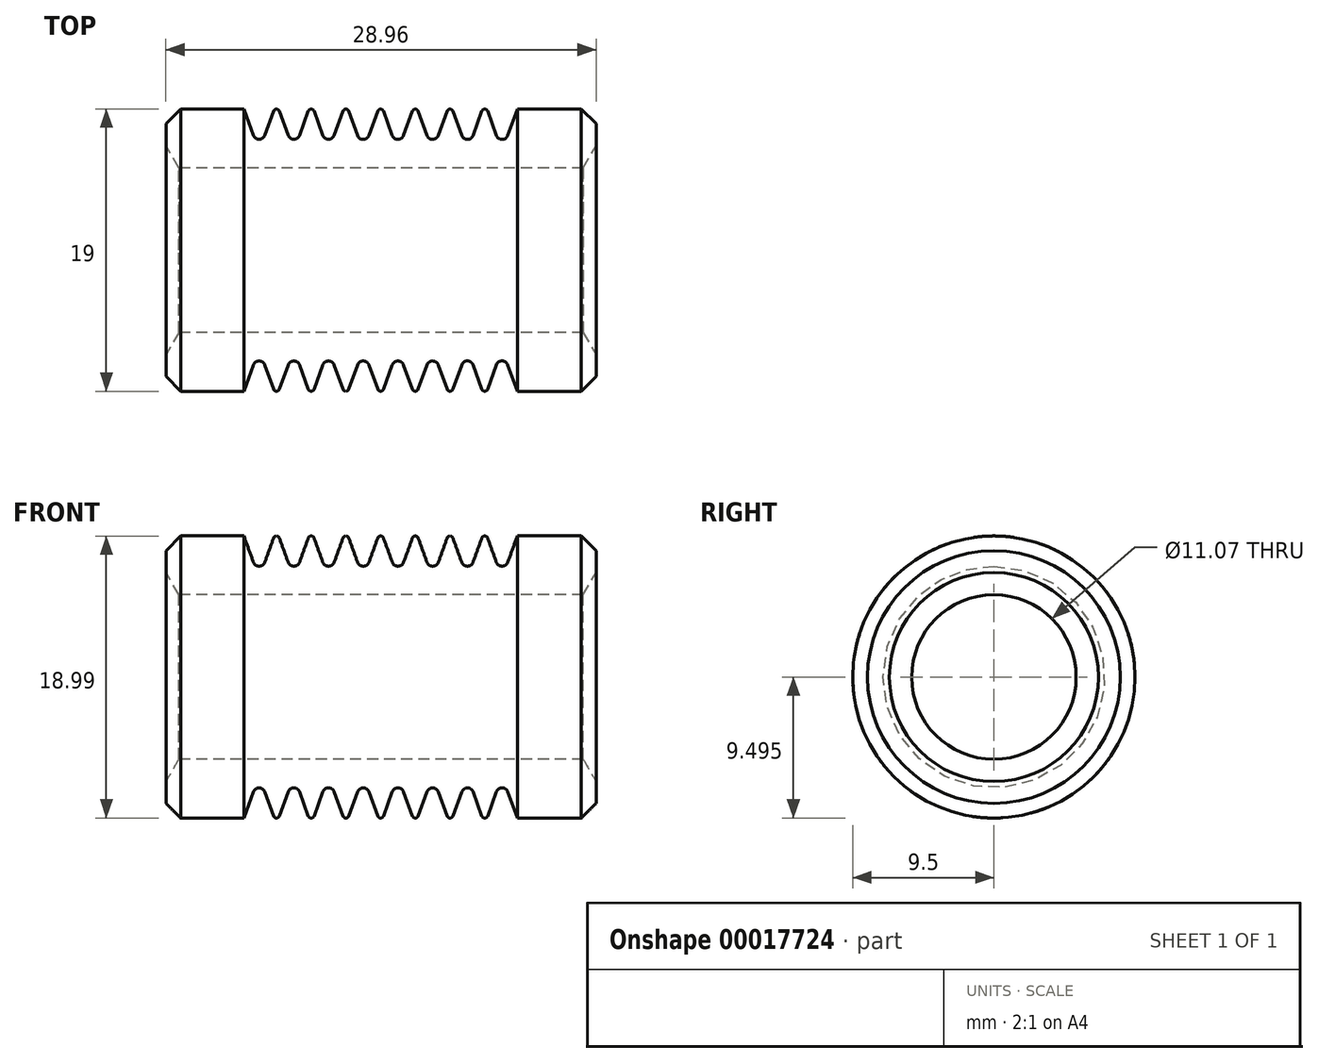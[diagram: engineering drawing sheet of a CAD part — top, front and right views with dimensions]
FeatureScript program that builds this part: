
annotation { "Feature Type Name" : "Feature", "Feature Type Description" : "" }
export const myFeature = defineFeature(function(context is Context, id is Id, definition is map)
    precondition{}
    {
        {
            var Q0;
            Q0=qCreatedBy(makeId("Front.planeOp"),FACE);
            var sketch = newSketch(context, id + "F0", { "sketchPlane" : qUnion([Q0])});
            skLineSegment(sketch, "E0", {"start": v(-8.72, 3.22) * mm, "end": v(-3.47, 3.22) * mm});
            skLineSegment(sketch, "E1", {"start": v(-3.47, 3.22) * mm, "end": v(-2.83, 1.45) * mm});
            skLineSegment(sketch, "E2", {"start": v(-2.06, 1.45) * mm, "end": v(-1.47, 3.1) * mm});
            skLineSegment(sketch, "E3", {"start": v(-3.47, 3.22) * mm, "end": v(15.19, 3.22) * mm, "construction": true});
            skLineSegment(sketch, "E4", {"start": v(-1.09, 3.1) * mm, "end": v(-0.5, 1.45) * mm});
            skLineSegment(sketch, "E5", {"start": v(0.27, 1.45) * mm, "end": v(0.87, 3.1) * mm});
            skLineSegment(sketch, "E6", {"start": v(1.25, 3.1) * mm, "end": v(1.85, 1.45) * mm});
            skLineSegment(sketch, "E7", {"start": v(2.61, 1.45) * mm, "end": v(3.2, 3.1) * mm});
            skLineSegment(sketch, "E8", {"start": v(3.59, 3.1) * mm, "end": v(4.18, 1.45) * mm});
            skLineSegment(sketch, "E9", {"start": v(4.95, 1.45) * mm, "end": v(5.54, 3.1) * mm});
            skLineSegment(sketch, "E10", {"start": v(5.92, 3.1) * mm, "end": v(6.52, 1.45) * mm});
            skLineSegment(sketch, "E11", {"start": v(7.28, 1.45) * mm, "end": v(7.88, 3.1) * mm});
            skLineSegment(sketch, "E12", {"start": v(8.26, 3.1) * mm, "end": v(8.86, 1.45) * mm});
            skLineSegment(sketch, "E13", {"start": v(9.62, 1.45) * mm, "end": v(10.22, 3.1) * mm});
            skLineSegment(sketch, "E14", {"start": v(10.6, 3.1) * mm, "end": v(11.2, 1.45) * mm});
            skLineSegment(sketch, "E15", {"start": v(11.96, 1.45) * mm, "end": v(12.55, 3.1) * mm});
            skLineSegment(sketch, "E16", {"start": v(12.93, 3.1) * mm, "end": v(13.53, 1.45) * mm});
            skLineSegment(sketch, "E17", {"start": v(14.3, 1.45) * mm, "end": v(14.94, 3.22) * mm});
            skLineSegment(sketch, "E18", {"start": v(14.94, 3.22) * mm, "end": v(20.24, 3.22) * mm});
            skLineSegment(sketch, "E19", {"start": v(20.24, 3.22) * mm, "end": v(20.24, -0.74) * mm});
            skLineSegment(sketch, "E20", {"start": v(-8.72, 3.22) * mm, "end": v(-8.72, -0.74) * mm});
            skLineSegment(sketch, "E21", {"start": v(20.24, -0.74) * mm, "end": v(-8.72, -0.74) * mm});
            skPoint(sketch, "E22.visualSharp", {"position": v(-1.13, 3.22) * mm});
            skArc(sketch, "E22.filletArc", {"start": v(-1.09, 3.1) * mm, "mid": v(-1.28, 3.22) * mm, "end": v(-1.47, 3.1) * mm});
            skPoint(sketch, "E23.visualSharp", {"position": v(1.06, 3.62) * mm});
            skArc(sketch, "E23.filletArc", {"start": v(1.25, 3.1) * mm, "mid": v(1.06, 3.22) * mm, "end": v(0.87, 3.1) * mm});
            skPoint(sketch, "E24.visualSharp", {"position": v(3.4, 3.62) * mm});
            skArc(sketch, "E24.filletArc", {"start": v(3.59, 3.1) * mm, "mid": v(3.4, 3.22) * mm, "end": v(3.2, 3.1) * mm});
            skPoint(sketch, "E25.visualSharp", {"position": v(5.73, 3.62) * mm});
            skArc(sketch, "E25.filletArc", {"start": v(5.92, 3.1) * mm, "mid": v(5.73, 3.22) * mm, "end": v(5.54, 3.1) * mm});
            skPoint(sketch, "E26.visualSharp", {"position": v(8.07, 3.22) * mm});
            skArc(sketch, "E26.filletArc", {"start": v(8.26, 3.1) * mm, "mid": v(8.07, 3.22) * mm, "end": v(7.88, 3.1) * mm});
            skPoint(sketch, "E27.visualSharp", {"position": v(10.4, 3.22) * mm});
            skArc(sketch, "E27.filletArc", {"start": v(10.6, 3.1) * mm, "mid": v(10.4, 3.22) * mm, "end": v(10.22, 3.1) * mm});
            skPoint(sketch, "E28.visualSharp", {"position": v(12.74, 3.22) * mm});
            skArc(sketch, "E28.filletArc", {"start": v(12.93, 3.1) * mm, "mid": v(12.74, 3.22) * mm, "end": v(12.55, 3.1) * mm});
            skPoint(sketch, "E29.visualSharp", {"position": v(-2.45, 0.4) * mm});
            skArc(sketch, "E29.filletArc", {"start": v(-2.83, 1.45) * mm, "mid": v(-2.45, 1.19) * mm, "end": v(-2.06, 1.45) * mm});
            skPoint(sketch, "E30.visualSharp", {"position": v(-0.1, 0.4) * mm});
            skArc(sketch, "E30.filletArc", {"start": v(-0.5, 1.45) * mm, "mid": v(-0.1, 1.19) * mm, "end": v(0.27, 1.45) * mm});
            skPoint(sketch, "E31.visualSharp", {"position": v(2.23, 0.4) * mm});
            skArc(sketch, "E31.filletArc", {"start": v(1.85, 1.45) * mm, "mid": v(2.23, 1.19) * mm, "end": v(2.61, 1.45) * mm});
            skPoint(sketch, "E32.visualSharp", {"position": v(4.57, 0.4) * mm});
            skArc(sketch, "E32.filletArc", {"start": v(4.18, 1.45) * mm, "mid": v(4.57, 1.19) * mm, "end": v(4.95, 1.45) * mm});
            skPoint(sketch, "E33.visualSharp", {"position": v(6.9, 0.4) * mm});
            skArc(sketch, "E33.filletArc", {"start": v(6.52, 1.45) * mm, "mid": v(6.9, 1.19) * mm, "end": v(7.28, 1.45) * mm});
            skPoint(sketch, "E34.visualSharp", {"position": v(9.24, 0.4) * mm});
            skArc(sketch, "E34.filletArc", {"start": v(8.86, 1.45) * mm, "mid": v(9.24, 1.19) * mm, "end": v(9.62, 1.45) * mm});
            skPoint(sketch, "E35.visualSharp", {"position": v(11.58, 0.4) * mm});
            skArc(sketch, "E35.filletArc", {"start": v(11.2, 1.45) * mm, "mid": v(11.58, 1.19) * mm, "end": v(11.96, 1.45) * mm});
            skPoint(sketch, "E36.visualSharp", {"position": v(13.91, 0.4) * mm});
            skArc(sketch, "E36.filletArc", {"start": v(13.53, 1.45) * mm, "mid": v(13.91, 1.19) * mm, "end": v(14.3, 1.45) * mm});
            skLineSegment(sketch, "E37", {"start": v(-2.45, 1.19) * mm, "end": v(13.91, 1.19) * mm, "construction": true});
            skLineSegment(sketch, "E38", {"start": v(-8.84, -6.28) * mm, "end": v(20.13, -6.28) * mm, "construction": true});
            skSolve(sketch);
        }
        {
            var Q0;
            Q0=makeQuery(id+"F0.imprint","IMPRINT",FACE,{"disambiguationData":[TD([[makeQuery(id+"F0.imprint","IMPRINT",EDGE,{"derivedFrom":sQuery(id+"F0.wireOp",EDGE,"E0")}),-1.0]])]});
            var Q1;
            Q1=sQuery(id+"F0.wireOp",EDGE,"E38");
            revolve(context, id + "F1", {"entities" : qUnion([Q0]), "axis" : qUnion([Q1]), "revolveType" : RevolveType.FULL});
        }
        {
            var Q0;
            Q0=makeQuery(id+"F1.opRevolve","SWEPT_EDGE",EDGE,{"disambiguationData":[OSD([sQuery(id+"F0.wireOp",EDGE,"E18"),sQuery(id+"F0.wireOp",EDGE,"E19")])]});
            var Q1;
            Q1=makeQuery(id+"F1.opRevolve","SWEPT_EDGE",EDGE,{"disambiguationData":[OSD([sQuery(id+"F0.wireOp",EDGE,"E0"),sQuery(id+"F0.wireOp",EDGE,"E20")])]});
            chamfer(context, id + "F2", {"entities" : qUnion([Q0, Q1]), "chamferType" : ChamferType.OFFSET_ANGLE, "width" : 1 * mm, "oppositeDirection" : false, "angle" : 45 * degree, "tangentPropagation" : true});
        }
        {
            var Q0;
            Q0=makeQuery(id+"F1.opRevolve","SWEPT_EDGE",EDGE,{"disambiguationData":[OSD([sQuery(id+"F0.wireOp",EDGE,"E19"),sQuery(id+"F0.wireOp",EDGE,"E21")])]});
            var Q1;
            Q1=makeQuery(id+"F1.opRevolve","SWEPT_EDGE",EDGE,{"disambiguationData":[OSD([sQuery(id+"F0.wireOp",EDGE,"E20"),sQuery(id+"F0.wireOp",EDGE,"E21")])]});
            chamfer(context, id + "F3", {"entities" : qUnion([Q0, Q1]), "chamferType" : ChamferType.OFFSET_ANGLE, "width" : 1.5 * mm, "oppositeDirection" : false, "angle" : 30 * degree, "tangentPropagation" : true});
        }
    });
